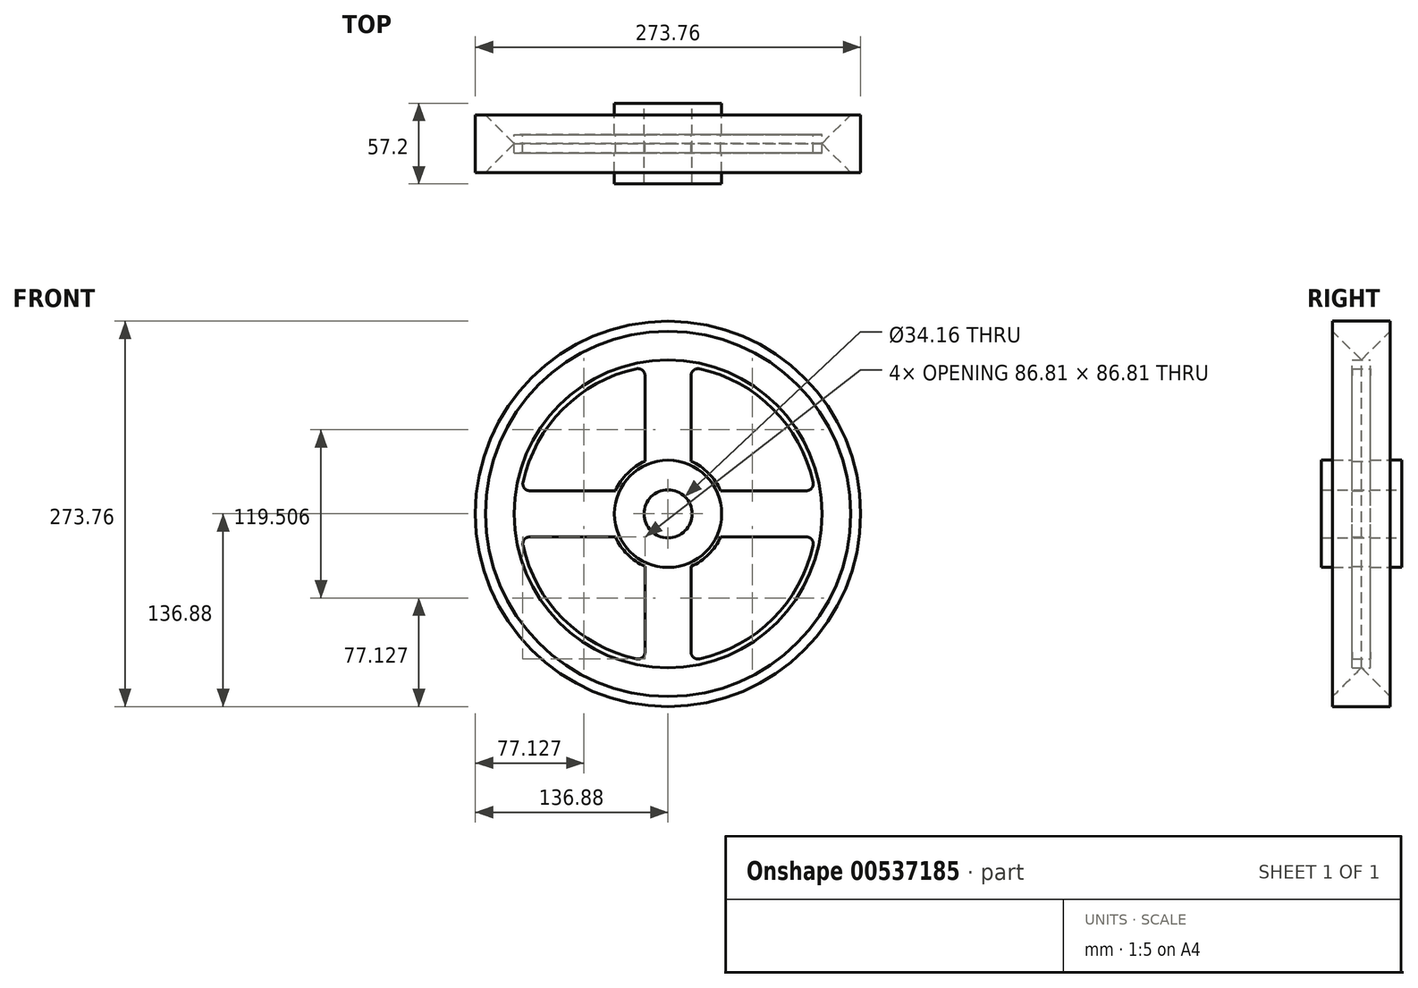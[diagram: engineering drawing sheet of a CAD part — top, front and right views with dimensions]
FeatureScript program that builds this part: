
annotation { "Feature Type Name" : "Feature", "Feature Type Description" : "" }
export const myFeature = defineFeature(function(context is Context, id is Id, definition is map)
    precondition{}
    {
        {
            var Q0;
            Q0=qCreatedBy(makeId("Front.planeOp"),FACE);
            var sketch = newSketch(context, id + "F0", { "sketchPlane" : qUnion([Q0])});
            skCircle(sketch, "E0", {"center": v(0, 0) * mm, "radius": 17.08 * mm});
            skCircle(sketch, "E1", {"center": v(0, 0) * mm, "radius": 38.1 * mm});
            skArc(sketch, "E2", {"start": v(-37.33, -16.35) * mm, "mid": v(-28.82, -28.82) * mm, "end": v(-16.35, -37.33) * mm});
            skCircle(sketch, "E3", {"center": v(0, 0) * mm, "radius": 109.28 * mm});
            skArc(sketch, "E4", {"start": v(22.41, -103.04) * mm, "mid": v(74.57, -74.57) * mm, "end": v(103.04, -22.41) * mm});
            skArc(sketch, "E5.trimOffspring", {"start": v(16.35, -37.33) * mm, "mid": v(28.82, -28.82) * mm, "end": v(37.33, -16.35) * mm});
            skArc(sketch, "E6.trimOffspring", {"start": v(37.33, 16.35) * mm, "mid": v(28.82, 28.82) * mm, "end": v(16.35, 37.33) * mm});
            skArc(sketch, "E7.trimOffspring", {"start": v(-16.35, 37.33) * mm, "mid": v(-28.82, 28.82) * mm, "end": v(-37.33, 16.35) * mm});
            skPoint(sketch, "E8.start.orphan", {"position": v(0, -40.75) * mm});
            skArc(sketch, "E9.trimOffspring", {"start": v(103.04, 22.41) * mm, "mid": v(74.57, 74.57) * mm, "end": v(22.41, 103.04) * mm});
            skArc(sketch, "E10.trimOffspring", {"start": v(-22.41, 103.04) * mm, "mid": v(-74.57, 74.57) * mm, "end": v(-103.04, 22.41) * mm});
            skArc(sketch, "E11.trimOffspring", {"start": v(-103.04, -22.41) * mm, "mid": v(-74.57, -74.57) * mm, "end": v(-22.41, -103.04) * mm});
            skLineSegment(sketch, "E12", {"start": v(-16.35, 98.16) * mm, "end": v(-16.35, 37.33) * mm});
            skLineSegment(sketch, "E13", {"start": v(-98.16, 16.35) * mm, "end": v(-37.33, 16.35) * mm});
            skLineSegment(sketch, "E14", {"start": v(-98.16, -16.35) * mm, "end": v(-37.33, -16.35) * mm});
            skLineSegment(sketch, "E15", {"start": v(-16.35, -98.16) * mm, "end": v(-16.35, -37.33) * mm});
            skLineSegment(sketch, "E16", {"start": v(16.35, -37.33) * mm, "end": v(16.35, -98.16) * mm});
            skLineSegment(sketch, "E17", {"start": v(37.33, -16.35) * mm, "end": v(98.16, -16.35) * mm});
            skLineSegment(sketch, "E18", {"start": v(37.33, 16.35) * mm, "end": v(98.16, 16.35) * mm});
            skLineSegment(sketch, "E19", {"start": v(16.35, 37.33) * mm, "end": v(16.35, 98.16) * mm});
            skPoint(sketch, "E20.visualSharp", {"position": v(-104.18, 16.35) * mm});
            skArc(sketch, "E20.filletArc", {"start": v(-103.04, 22.41) * mm, "mid": v(-102.05, 18.21) * mm, "end": v(-98.16, 16.35) * mm});
            skPoint(sketch, "E21.visualSharp", {"position": v(-16.35, 104.18) * mm});
            skArc(sketch, "E21.filletArc", {"start": v(-16.35, 98.16) * mm, "mid": v(-18.21, 102.05) * mm, "end": v(-22.41, 103.04) * mm});
            skPoint(sketch, "E22.visualSharp", {"position": v(16.35, 104.18) * mm});
            skArc(sketch, "E22.filletArc", {"start": v(22.41, 103.04) * mm, "mid": v(18.21, 102.05) * mm, "end": v(16.35, 98.16) * mm});
            skPoint(sketch, "E23.visualSharp", {"position": v(104.18, 16.35) * mm});
            skArc(sketch, "E23.filletArc", {"start": v(98.16, 16.35) * mm, "mid": v(102.05, 18.21) * mm, "end": v(103.04, 22.41) * mm});
            skPoint(sketch, "E24.visualSharp", {"position": v(104.18, -16.35) * mm});
            skArc(sketch, "E24.filletArc", {"start": v(103.04, -22.41) * mm, "mid": v(102.05, -18.21) * mm, "end": v(98.16, -16.35) * mm});
            skPoint(sketch, "E25.visualSharp", {"position": v(16.35, -104.18) * mm});
            skArc(sketch, "E25.filletArc", {"start": v(16.35, -98.16) * mm, "mid": v(18.21, -102.05) * mm, "end": v(22.41, -103.04) * mm});
            skPoint(sketch, "E26.visualSharp", {"position": v(-16.35, -104.18) * mm});
            skArc(sketch, "E26.filletArc", {"start": v(-22.41, -103.04) * mm, "mid": v(-18.21, -102.05) * mm, "end": v(-16.35, -98.16) * mm});
            skPoint(sketch, "E27.visualSharp", {"position": v(-104.18, -16.35) * mm});
            skArc(sketch, "E27.filletArc", {"start": v(-98.16, -16.35) * mm, "mid": v(-102.05, -18.21) * mm, "end": v(-103.04, -22.41) * mm});
            skSolve(sketch);
        }
        {
            var Q0;
            Q0 = qSketchRegion(id + "F0", true);
            extrude(context, id + "F1", {"entities" : qUnion([Q0]), "endBound" : BoundingType.SYMMETRIC, "depth" : 13 * mm, "offsetDistance" : 25 * mm});
        }
        {
            var Q0;
            Q0=makeQuery(id+"F0.imprint","IMPRINT",FACE,{"disambiguationData":[TD([[makeQuery(id+"F0.imprint","IMPRINT",EDGE,{"derivedFrom":sQuery(id+"F0.wireOp",EDGE,"E0")}),-1.0]])]});
            extrude(context, id + "F2", {"entities" : qUnion([Q0]), "operationType" : NewBodyOperationType.ADD, "endBound" : BoundingType.SYMMETRIC, "depth" : 57.2 * mm, "offsetDistance" : 25 * mm});
        }
        {
            var Q0;
            Q0=makeQuery(id+"F0.imprint","IMPRINT",FACE,{"disambiguationData":[TD([[makeQuery(id+"F0.imprint","IMPRINT",EDGE,{"derivedFrom":sQuery(id+"F0.wireOp",EDGE,"E0")}),1.0]])]});
            var sketch = newSketch(context, id + "F3", { "sketchPlane" : qUnion([Q0])});
            skCircle(sketch, "E28", {"center": v(0, 0) * mm, "radius": 130.7 * mm});
            skCircle(sketch, "E29", {"center": v(0, 0) * mm, "radius": 109.28 * mm});
            skCircle(sketch, "E30", {"center": v(0, 0) * mm, "radius": 136.88 * mm});
            skSolve(sketch);
        }
        {
            var Q0;
            Q0=makeQuery(id+"F3.imprint","IMPRINT",FACE,{"disambiguationData":[TD([[makeQuery(id+"F3.imprint","IMPRINT",EDGE,{"derivedFrom":sQuery(id+"F3.wireOp",EDGE,"E28")}),1.0]])]});
            extrude(context, id + "F4", {"entities" : qUnion([Q0]), "endBound" : BoundingType.SYMMETRIC, "depth" : 41 * mm, "offsetDistance" : 25 * mm});
        }
        {
            var Q0;
            Q0=makeQuery(id+"F4.opExtrude","SWEPT_FACE",FACE,{"disambiguationData":[OSD([sQuery(id+"F3.wireOp",EDGE,"E29")])]});
            chamfer(context, id + "F5", {"entities" : qUnion([Q0]), "width" : 20.5 * mm, "tangentPropagation" : true});
        }
        {
            var Q0;
            Q0=makeQuery(id+"F3.imprint","IMPRINT",FACE,{"disambiguationData":[TD([[makeQuery(id+"F3.imprint","IMPRINT",EDGE,{"derivedFrom":sQuery(id+"F3.wireOp",EDGE,"E28")}),-1.0]])]});
            extrude(context, id + "F6", {"entities" : qUnion([Q0]), "operationType" : NewBodyOperationType.ADD, "endBound" : BoundingType.SYMMETRIC, "depth" : 41 * mm, "offsetDistance" : 25 * mm});
        }
    });
